# Revit family: Worksurface-Teknion-JNWDG_Double-Sided_Writable_Glass-R2018
name_source: partatom
category: Furniture
revit_build: Autodesk Revit 2018 (Build: 20190510_1515(x64)
units: mm (PartAtom-declared; Revit-internal decimal feet)

## family parameters
Always vertical = Yes
Cut with Voids When Loaded = No
OmniClass Number = 23.40.20.00
OmniClass Title = General Furniture and Specialties
Room Calculation Point = No
Shared = Yes
Work Plane-Based = No

## types (3) — shared parameters
Assembly Code = E2020200
Manufacturer = Teknion
Manufacturer Fax = 416.661.4586
Part Number = JNWDG
Product Documentation Link = https://www.teknion.com
Product Line = Expansion Cityline
Product Page URL = https://www.teknion.com
Series = Expansion Cityline
Sustainability Data = https://www.teknion.com
URL = www.teknion.com
Unit Weight URL = http://www.teknion.com
Warranty = http://www.teknion.com

## per-type parameters (varying)
| type | Depth | Description | Model |
| 36" Depth, With Companion Marker Kit | 36 " | Double-Sided Writable Glass Worksurface, 36" Depth, With Companion Marker Kit | JNWDG36__K |
| 48" Depth, With Companion Marker Kit | 48 " | Double-Sided Writable Glass Worksurface, 48" Depth, With Companion Marker Kit | JNWDG48__K |
| 60" Depth, With Companion Marker Kit | 60 " | Double-Sided Writable Glass Worksurface, 60" Depth, With Companion Marker Kit | JNWDG60__K |

## geometry (parser evidence)
native form markers: Sweep x1
no freeform markers — native parametric forms only
